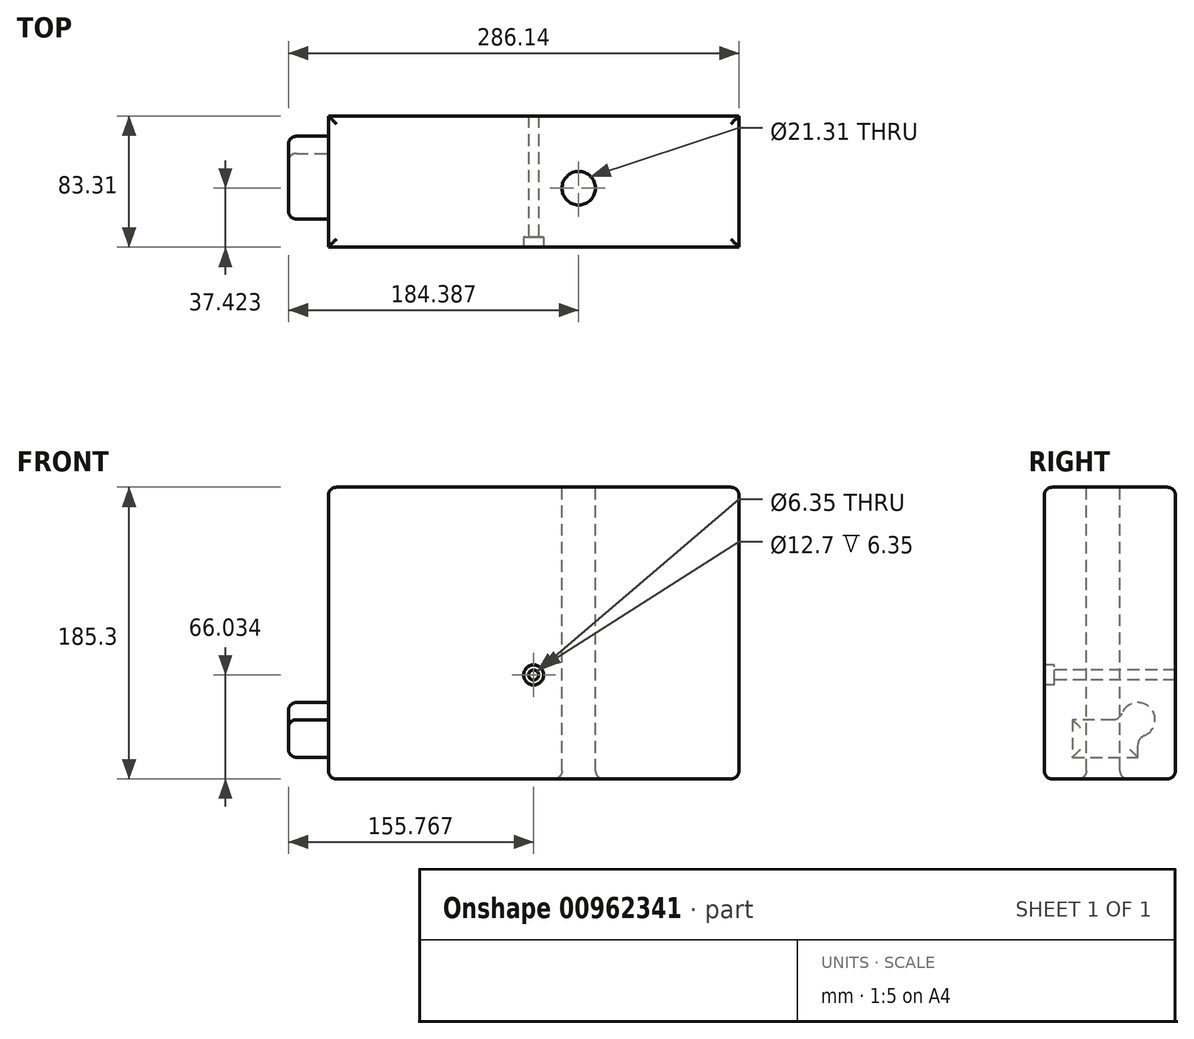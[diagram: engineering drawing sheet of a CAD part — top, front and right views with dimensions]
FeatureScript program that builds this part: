
annotation { "Feature Type Name" : "Feature", "Feature Type Description" : "" }
export const myFeature = defineFeature(function(context is Context, id is Id, definition is map)
    precondition{}
    {
        {
            var Q0;
            Q0=qCreatedBy(makeId("Front.planeOp"),FACE);
            var sketch = newSketch(context, id + "F0", { "sketchPlane" : qUnion([Q0])});
            skLineSegment(sketch, "E0.bottom", {"start": v(-148.91, 98.26) * mm, "end": v(111.83, 98.26) * mm});
            skLineSegment(sketch, "E0.top", {"start": v(-148.91, -87.04) * mm, "end": v(111.83, -87.04) * mm});
            skLineSegment(sketch, "E0.left", {"start": v(-148.91, 98.26) * mm, "end": v(-148.91, -87.04) * mm});
            skLineSegment(sketch, "E0.right", {"start": v(111.83, 98.26) * mm, "end": v(111.83, -87.04) * mm});
            skSolve(sketch);
        }
        {
            var Q0;
            Q0=makeQuery(id+"F0.imprint","IMPRINT",FACE,{"disambiguationData":[TD([[makeQuery(id+"F0.imprint","IMPRINT",EDGE,{"derivedFrom":sQuery(id+"F0.wireOp",EDGE,"E0.bottom")}),-1.0]])]});
            extrude(context, id + "F1", {"entities" : qUnion([Q0]), "depth" : 83.31 * mm, "offsetDistance" : 25.4 * mm});
        }
        {
            var Q0;
            Q0=makeQuery(id+"F1.opExtrude","SWEPT_EDGE",EDGE,{"disambiguationData":[OSD([sQuery(id+"F0.wireOp",EDGE,"E0.bottom"),sQuery(id+"F0.wireOp",EDGE,"E0.left")])]});
            var Q1;
            Q1=makeQuery(id+"F1.opExtrude","CAP_EDGE",EDGE,{"disambiguationData":[OSD([sQuery(id+"F0.wireOp",EDGE,"E0.bottom")])],"isStart":false});
            var Q2;
            Q2=makeQuery(id+"F1.opExtrude","SWEPT_EDGE",EDGE,{"disambiguationData":[OSD([sQuery(id+"F0.wireOp",EDGE,"E0.bottom"),sQuery(id+"F0.wireOp",EDGE,"E0.right")])]});
            var Q3;
            Q3=makeQuery(id+"F1.opExtrude","CAP_EDGE",EDGE,{"disambiguationData":[OSD([sQuery(id+"F0.wireOp",EDGE,"E0.bottom")])],"isStart":true});
            fillet(context, id + "F2", {"entities" : qUnion([Q0, Q1, Q2, Q3]), "radius" : 5.08 * mm, "tangentPropagation" : true, "allowEdgeOverflow" : false});
        }
        {
            var Q0;
            Q0=makeQuery(id+"F1.opExtrude","SWEPT_FACE",FACE,{"disambiguationData":[OSD([sQuery(id+"F0.wireOp",EDGE,"E0.bottom")])]});
            var sketch = newSketch(context, id + "F3", { "sketchPlane" : qUnion([Q0])});
            skCircle(sketch, "E1", {"center": v(10.08, -45.89) * mm, "radius": 10.66 * mm});
            skSolve(sketch);
        }
        {
            var Q0;
            Q0=makeQuery(id+"F3.imprint","IMPRINT",FACE,{"disambiguationData":[TD([[makeQuery(id+"F3.imprint","IMPRINT",EDGE,{"derivedFrom":sQuery(id+"F3.wireOp",EDGE,"E1")}),1.0]])]});
            extrude(context, id + "F4", {"entities" : qUnion([Q0]), "operationType" : NewBodyOperationType.REMOVE, "endBound" : BoundingType.UP_TO_NEXT, "oppositeDirection" : true, "depth" : 25.4 * mm, "offsetDistance" : 25.4 * mm});
        }
        {
            var Q0;
            Q0=makeQuery(id+"F1.opExtrude","SWEPT_FACE",FACE,{"disambiguationData":[OSD([sQuery(id+"F0.wireOp",EDGE,"E0.left")])]});
            var sketch = newSketch(context, id + "F5", { "sketchPlane" : qUnion([Q0])});
            skArc(sketch, "E2", {"start": v(33.92, -45.4) * mm, "mid": v(16.08, -41.72) * mm, "end": v(19.78, -59.55) * mm});
            skLineSegment(sketch, "E3", {"start": v(39.83, -49.42) * mm, "end": v(65.43, -49.42) * mm});
            skLineSegment(sketch, "E4", {"start": v(65.43, -49.42) * mm, "end": v(65.43, -73.27) * mm});
            skLineSegment(sketch, "E5", {"start": v(65.43, -73.27) * mm, "end": v(23.79, -73.27) * mm});
            skLineSegment(sketch, "E6", {"start": v(23.79, -73.27) * mm, "end": v(23.79, -65.46) * mm});
            skPoint(sketch, "E7.visualSharp", {"position": v(34.69, -49.42) * mm});
            skArc(sketch, "E7.filletArc", {"start": v(33.92, -45.4) * mm, "mid": v(36.26, -48.32) * mm, "end": v(39.83, -49.42) * mm});
            skPoint(sketch, "E8.visualSharp", {"position": v(23.79, -60.32) * mm});
            skArc(sketch, "E8.filletArc", {"start": v(23.79, -65.46) * mm, "mid": v(22.7, -61.89) * mm, "end": v(19.78, -59.55) * mm});
            skSolve(sketch);
        }
        {
            var Q0;
            Q0 = qSketchRegion(id + "F5", true);
            extrude(context, id + "F6", {"entities" : qUnion([Q0]), "operationType" : NewBodyOperationType.ADD, "depth" : 25.4 * mm, "offsetDistance" : 25.4 * mm});
        }
        {
            var Q0;
            Q0=makeQuery(id+"F6.opExtrude","CAP_FACE",FACE,{"disambiguationData":[OSD([sQuery(id+"F5.wireOp",EDGE,"E2"),sQuery(id+"F5.wireOp",EDGE,"E3"),sQuery(id+"F5.wireOp",EDGE,"E4"),sQuery(id+"F5.wireOp",EDGE,"E5"),sQuery(id+"F5.wireOp",EDGE,"E6"),sQuery(id+"F5.wireOp",EDGE,"E7.filletArc"),sQuery(id+"F5.wireOp",EDGE,"E8.filletArc")])],"isStart":false});
            var Q1;
            Q1=makeQuery(id+"F1.opExtrude","SWEPT_FACE",FACE,{"disambiguationData":[OSD([sQuery(id+"F0.wireOp",EDGE,"E0.top")])]});
            fillet(context, id + "F7", {"entities" : qUnion([Q0, Q1]), "radius" : 5.08 * mm, "tangentPropagation" : true, "allowEdgeOverflow" : false});
        }
        {
            var Q0;
            Q0=makeQuery(id+"F1.opExtrude","CAP_FACE",FACE,{"disambiguationData":[OSD([sQuery(id+"F0.wireOp",EDGE,"E0.bottom"),sQuery(id+"F0.wireOp",EDGE,"E0.top"),sQuery(id+"F0.wireOp",EDGE,"E0.left"),sQuery(id+"F0.wireOp",EDGE,"E0.right")])],"isStart":false});
            var sketch = newSketch(context, id + "F8", { "sketchPlane" : qUnion([Q0])});
            skLineSegment(sketch, "E9", {"start": v(-13.05, 5.61) * mm, "end": v(32.14, 5.61) * mm, "construction": true});
            skLineSegment(sketch, "E10", {"start": v(-18.54, 23.14) * mm, "end": v(-18.54, -21) * mm, "construction": true});
            skSolve(sketch);
        }
        {
            var Q0;
            Q0=sQuery(id+"F8.wireOp",VERTEX,"E10.end");
            var Q1;
            Q1=makeQuery(id+"F1.opExtrude","SWEPT_BODY",BODY,{"disambiguationData":[OSD([sQuery(id+"F0.wireOp",EDGE,"E0.bottom"),sQuery(id+"F0.wireOp",EDGE,"E0.top"),sQuery(id+"F0.wireOp",EDGE,"E0.left"),sQuery(id+"F0.wireOp",EDGE,"E0.right")])]});
            hole(context, id + "F9", {"style" : HoleStyle.C_BORE, "endStyle" : HoleEndStyle.THROUGH, "holeDiameter" : 6.35 * mm, "cBoreDiameter" : 12.7 * mm, "cBoreDepth" : 6.35 * mm, "majorDiameter" : 6.35 * mm, "isTappedThrough" : true, "tappedDepth" : 12.7 * mm, "tapClearance" : 3, "locations" : qUnion([Q0]), "scope" : qUnion([Q1])});
        }
        {
            var Q0;
            Q0=qCreatedBy(makeId("Right.planeOp"),FACE);
            var sketch = newSketch(context, id + "F10", { "sketchPlane" : qUnion([Q0])});
            skLineSegment(sketch, "E11", {"start": v(0, 0) * mm, "end": v(-137.17, 0) * mm, "construction": true});
            skSolve(sketch);
        }
    });
